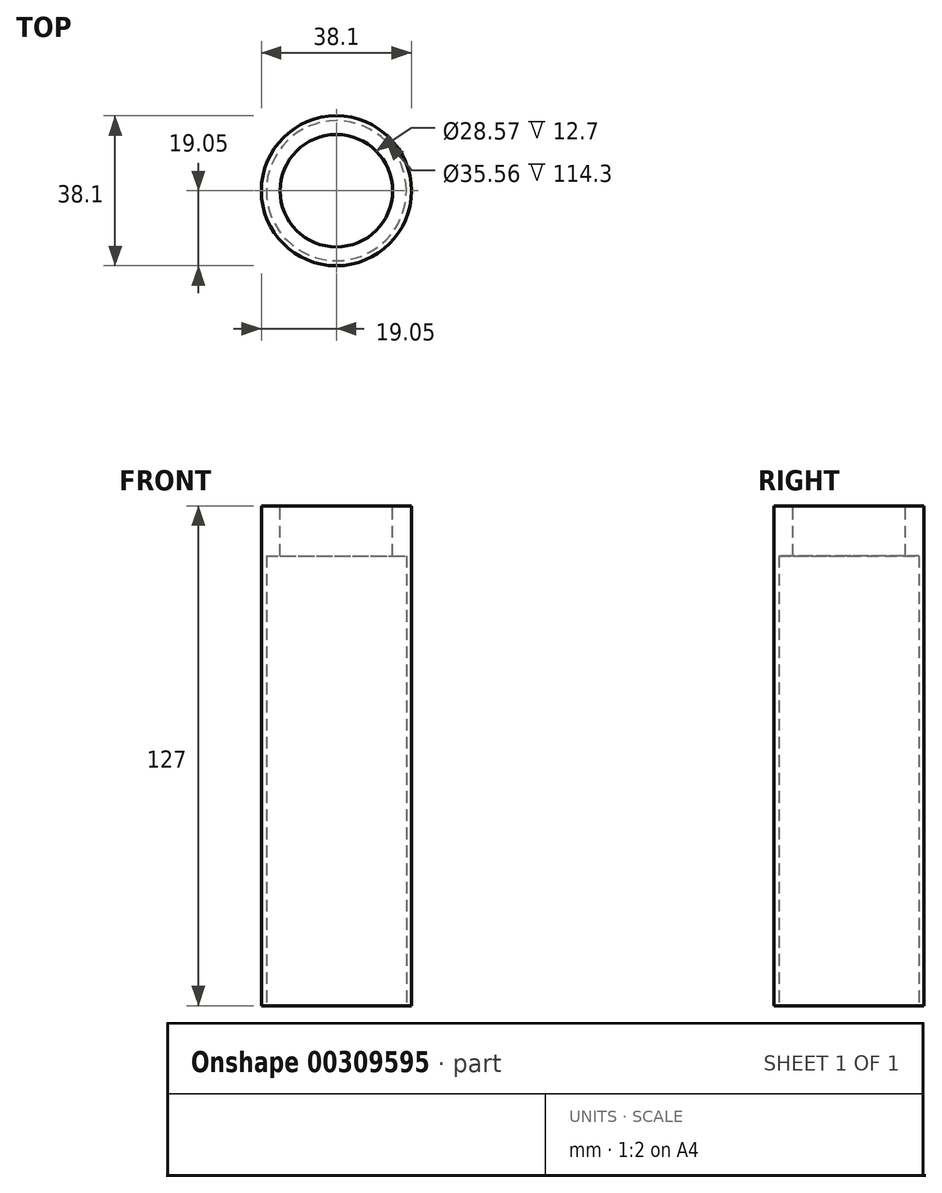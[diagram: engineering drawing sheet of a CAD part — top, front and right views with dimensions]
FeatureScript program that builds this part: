
annotation { "Feature Type Name" : "Feature", "Feature Type Description" : "" }
export const myFeature = defineFeature(function(context is Context, id is Id, definition is map)
    precondition{}
    {
        {
            var Q0;
            Q0=qCreatedBy(makeId("Top.planeOp"),FACE);
            var sketch = newSketch(context, id + "F0", { "sketchPlane" : qUnion([Q0])});
            skCircle(sketch, "E0", {"center": v(0, 0) * mm, "radius": 19.05 * mm});
            skSolve(sketch);
        }
        {
            var Q0;
            Q0 = qSketchRegion(id + "F0", true);
            extrude(context, id + "F1", {"entities" : qUnion([Q0]), "depth" : 127 * mm});
        }
        {
            var Q0;
            Q0=makeQuery(id+"F1.opExtrude","CAP_FACE",FACE,{"disambiguationData":[OSD([sQuery(id+"F0.wireOp",EDGE,"E0")])],"isStart":false});
            var sketch = newSketch(context, id + "F2", { "sketchPlane" : qUnion([Q0])});
            skCircle(sketch, "E1", {"center": v(0, 0) * mm, "radius": 14.29 * mm});
            skSolve(sketch);
        }
        {
            var Q0;
            Q0 = qSketchRegion(id + "F2", true);
            extrude(context, id + "F3", {"entities" : qUnion([Q0]), "operationType" : NewBodyOperationType.REMOVE, "endBound" : BoundingType.THROUGH_ALL, "oppositeDirection" : true, "depth" : 25.4 * mm});
        }
        {
            var Q0;
            Q0=makeQuery(id+"F1.opExtrude","CAP_FACE",FACE,{"disambiguationData":[OSD([sQuery(id+"F0.wireOp",EDGE,"E0")])],"isStart":true});
            var sketch = newSketch(context, id + "F4", { "sketchPlane" : qUnion([Q0])});
            skCircle(sketch, "E2", {"center": v(0, 0) * mm, "radius": 17.78 * mm});
            skSolve(sketch);
        }
        {
            var Q0;
            Q0 = qSketchRegion(id + "F4", true);
            extrude(context, id + "F5", {"entities" : qUnion([Q0]), "operationType" : NewBodyOperationType.REMOVE, "oppositeDirection" : true, "depth" : 114.3 * mm});
        }
    });
